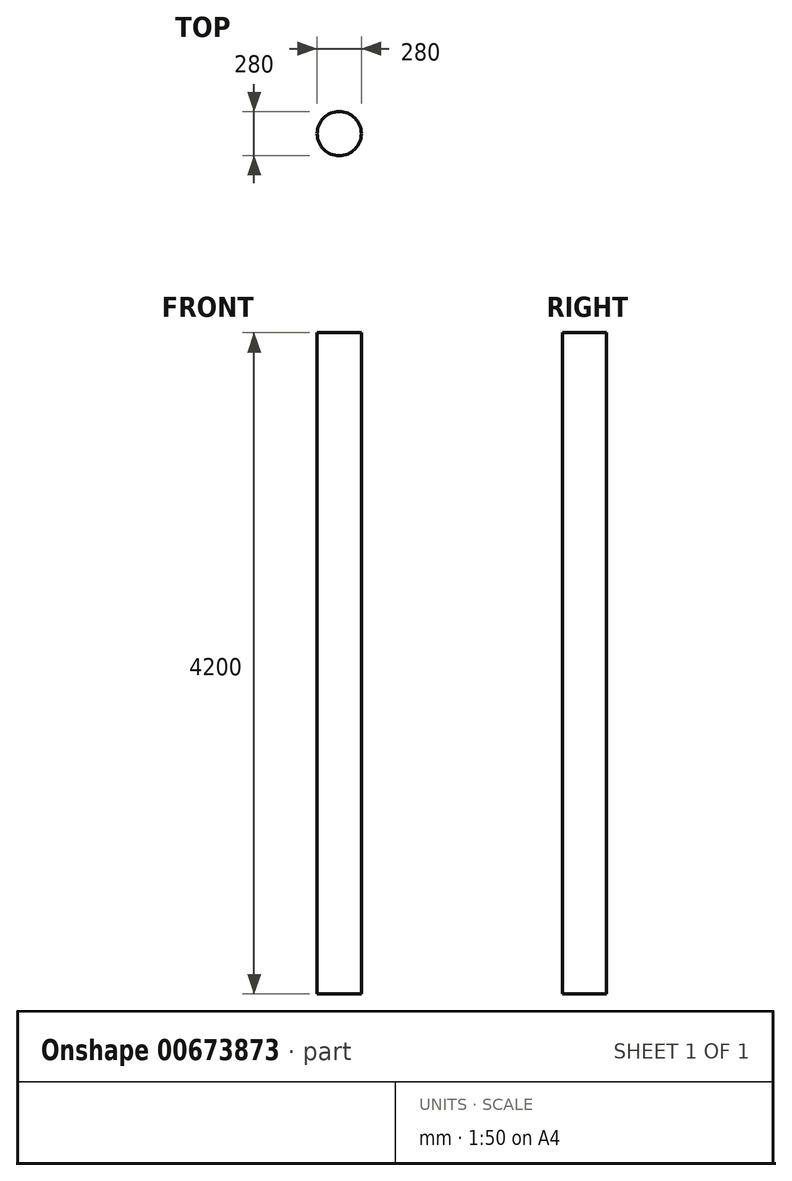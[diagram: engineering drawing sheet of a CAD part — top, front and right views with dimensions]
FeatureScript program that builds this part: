
annotation { "Feature Type Name" : "Feature", "Feature Type Description" : "" }
export const myFeature = defineFeature(function(context is Context, id is Id, definition is map)
    precondition{}
    {
        {
            var Q0;
            Q0=qCreatedBy(makeId("Top.planeOp"),FACE);
            var sketch = newSketch(context, id + "F0", { "sketchPlane" : qUnion([Q0])});
            skCircle(sketch, "E0", {"center": v(-45.22, 31.73) * mm, "radius": 140 * mm});
            skSolve(sketch);
        }
        {
            var Q0;
            Q0=makeQuery(id+"F0.imprint","IMPRINT",FACE,{"disambiguationData":[TD([[makeQuery(id+"F0.imprint","IMPRINT",EDGE,{"derivedFrom":sQuery(id+"F0.wireOp",EDGE,"E0")}),1.0]])]});
            extrude(context, id + "F1", {"entities" : qUnion([Q0]), "depth" : 3000 * mm, "offsetDistance" : 25 * mm});
        }
        {
            var Q0;
            Q0=makeQuery(id+"F1.opExtrude","CAP_FACE",FACE,{"disambiguationData":[OSD([sQuery(id+"F0.wireOp",EDGE,"E0")])],"isStart":true});
            extrude(context, id + "F2", {"entities" : qUnion([Q0]), "operationType" : NewBodyOperationType.ADD, "depth" : 1200 * mm, "offsetDistance" : 25 * mm});
        }
    });
